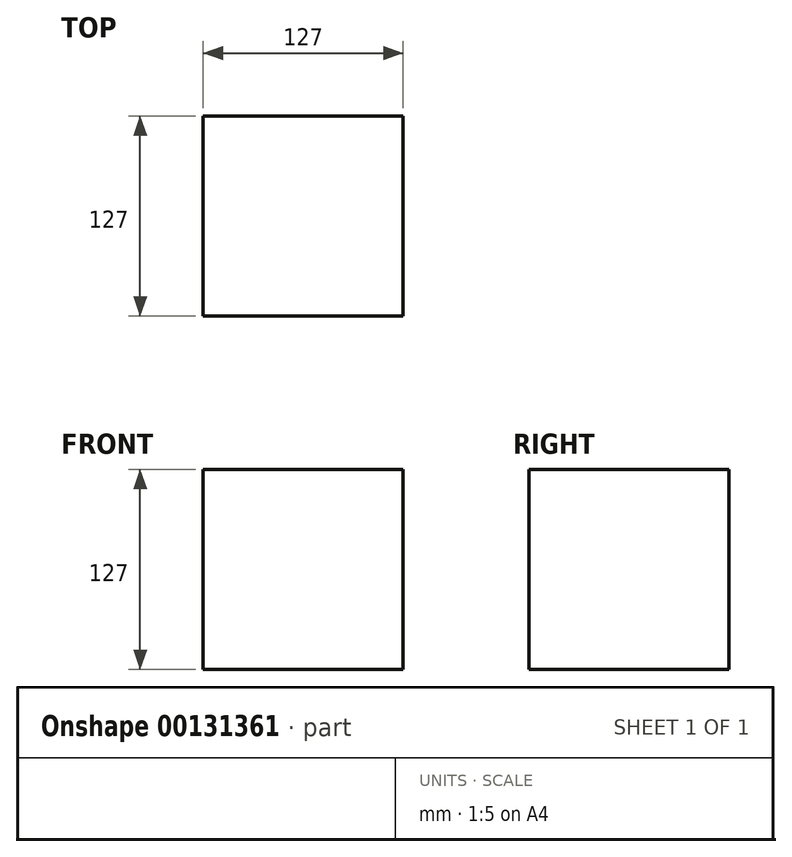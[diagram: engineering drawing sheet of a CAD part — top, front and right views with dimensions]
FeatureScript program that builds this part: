
annotation { "Feature Type Name" : "Feature", "Feature Type Description" : "" }
export const myFeature = defineFeature(function(context is Context, id is Id, definition is map)
    precondition{}
    {
        {
            var Q0;
            Q0=qCreatedBy(makeId("Top.planeOp"),FACE);
            var sketch = newSketch(context, id + "F0", { "sketchPlane" : qUnion([Q0])});
            skLineSegment(sketch, "E0.bottom", {"start": v(63.5, -63.5) * mm, "end": v(-63.5, -63.5) * mm});
            skLineSegment(sketch, "E0.top", {"start": v(63.5, 63.5) * mm, "end": v(-63.5, 63.5) * mm});
            skLineSegment(sketch, "E0.left", {"start": v(63.5, -63.5) * mm, "end": v(63.5, 63.5) * mm});
            skLineSegment(sketch, "E0.right", {"start": v(-63.5, -63.5) * mm, "end": v(-63.5, 63.5) * mm});
            skPoint(sketch, "E0.middle", {"position": v(0, 0) * mm});
            skSolve(sketch);
        }
        {
            var Q0;
            Q0 = qSketchRegion(id + "F0", true);
            extrude(context, id + "F1", {"entities" : qUnion([Q0]), "depth" : 127 * mm});
        }
    });
